# Revit family: Toilet-Wall_Mount-KOHLER-K-32410IN-1
name_source: partatom
category: Plumbing Fixtures
units: mm (PartAtom-declared; Revit-internal decimal feet)

## family parameters
Cut with Voids When Loaded = No
Host = Face
Maintain Annotation Orientation = No
OmniClass Number = 23.31.19.00
OmniClass Title = Toilets
Part Type = Normal
Room Calculation Point = No
Round Connector Dimension = Use Diameter
Shared = No

## types (2) — shared parameters
ADA Compliant = No
Assembly Code = D2010100
CW Connection = Yes
Cold Water Inlet = Cold Water Inlet
Date Modified = 02/03/2025
Default Elevation = 0"
Description = APT Square Wall Hung Bowl With Polypropylene Seat White
Flow Rate = 0 GPM
Flush Rate- GPF = GPF
Flush Rate- LPF = LPF
HW Connection = No
Height = 15 15/16"
Hot Water Inlet = Hot Water Inlet
Length = 21 5/16"
Manufacturer = Kohler Co.
Master Format 2014 = 22 42 13.13
Master Format 2014 Name = Residential Water Closets
Material = Vitreous China
Pressure = 0.00 psi
Seat Included = Yes
Secondary Finish = Kohler-Plastic-0-White
URL = https://www.kohler.co.in
Vent Connection = No
Waste Connection = Yes
Waste Water Outlet = Waste Water Outlet
WaterSense Certified = No
Width = 14 3/8"

## per-type parameters (varying)
| type | Finish | Model | Type |
| 0-White | Kohler-Vitreous_China-0-White | K-32410IN-0 | 1 |
| K4-Cashmere | Kohler-Vitreous_China-K4-Cashmere | K-32410IN-K4 | 2 |

## geometry (parser evidence)
native form markers: Sweep x5
no freeform markers — native parametric forms only
